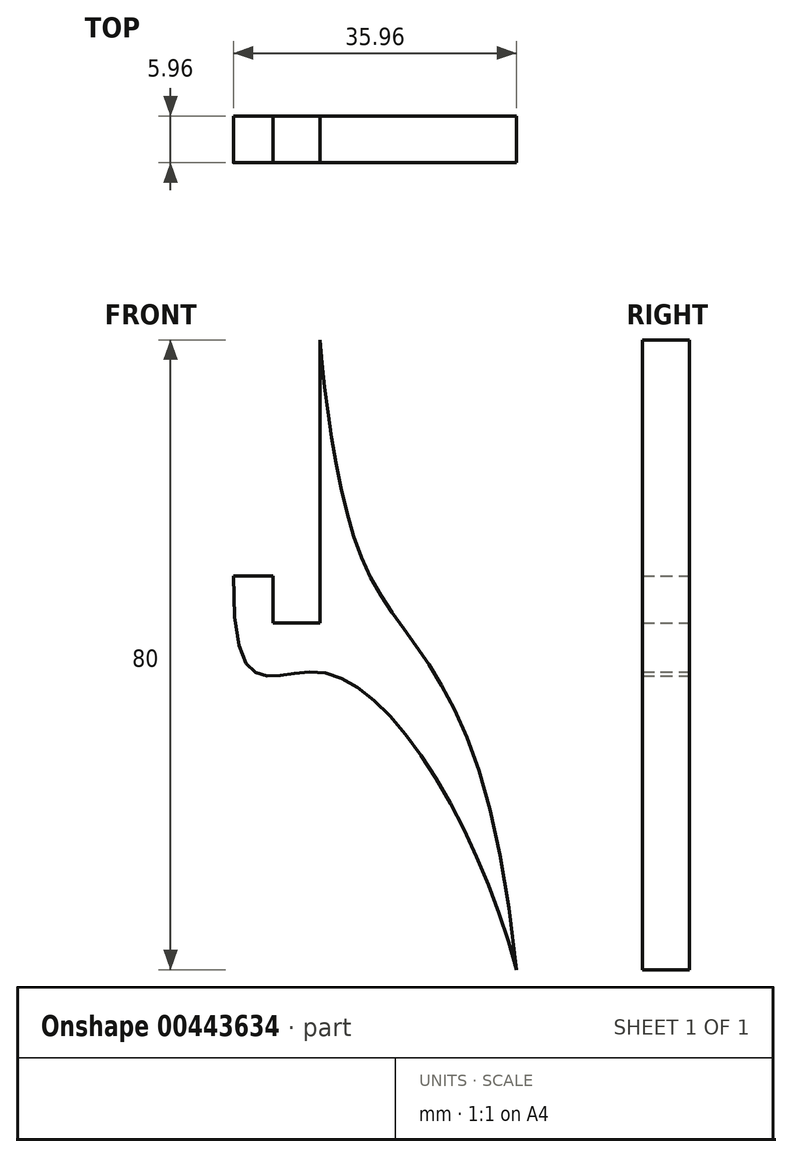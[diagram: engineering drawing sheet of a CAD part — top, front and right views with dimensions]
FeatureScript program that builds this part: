
annotation { "Feature Type Name" : "Feature", "Feature Type Description" : "" }
export const myFeature = defineFeature(function(context is Context, id is Id, definition is map)
    precondition{}
    {
        {
            var Q0;
            Q0=qCreatedBy(makeId("Front.planeOp"),FACE);
            var sketch = newSketch(context, id + "F0", { "sketchPlane" : qUnion([Q0])});
            skLineSegment(sketch, "E0", {"start": v(0, 0) * mm, "end": v(0, 30) * mm});
            skLineSegment(sketch, "E1", {"start": v(-10.96, 0) * mm, "end": v(-5.96, 0) * mm});
            skLineSegment(sketch, "E2", {"start": v(-5.96, 0) * mm, "end": v(-5.96, -5.96) * mm});
            skLineSegment(sketch, "E3", {"start": v(-5.96, -5.96) * mm, "end": v(0, -5.96) * mm});
            skLineSegment(sketch, "E4", {"start": v(0, -5.96) * mm, "end": v(0, 0) * mm});
            skFitSpline(sketch, "E5", {"points": [v(0, 30) * mm, v(6.36, 0) * mm, v(25, -50) * mm], "startDerivative": vector(6.22, -65.32) * mm, "endDerivative": vector(19.89, -193.2) * mm});
            skFitSpline(sketch, "E6", {"points": [v(-10.96, 0) * mm, v(0, -12.22) * mm, v(25, -50) * mm], "startDerivative": vector(-1.3, -141.03) * mm, "endDerivative": vector(21.55, -81.19) * mm});
            skSolve(sketch);
        }
        {
            var Q0;
            Q0 = qSketchRegion(id + "F0", true);
            extrude(context, id + "F1", {"entities" : qUnion([Q0]), "depth" : 5.96 * mm});
        }
    });
